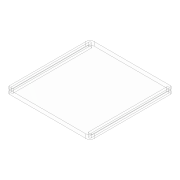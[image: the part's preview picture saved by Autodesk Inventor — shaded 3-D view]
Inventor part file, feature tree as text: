
AUTODESK INVENTOR PART (.ipt)
format: ipt  version: 2020 (Build 240168000, 168)  size: 138,752 bytes
history: native  units: mm
features: sketch x4, extrude x3, fillet x1, plane x1, mirror x1
ambient origin geometry x8: Origin, YZ Plane, XZ Plane, XY Plane, X Axis, Y Axis, Z Axis, Center Point
bodies: Solid1 (feature_tree)
feature tree (10):
  extrude  "Extrusion1"  Depth=105.0mm
  fillet  "Fillet1"  Radius=5.0mm
  sketch  "Sketch3"  dims[d10=5.0mm d11=2.5mm]
  extrude  "Extrusion3"  Depth=2.5mm
  extrude  "Extrusion4"  Depth=2.5mm
  plane  "Work Plane1"
  mirror  "Mirror1"
  sketch  "Sketch1"  dims[d0=105.0mm d1=105.0mm d2=5.0mm d3=0.0mm]
  sketch  "Sketch4"  dims[d12=2.5mm d13=2.5mm]
  sketch  "Sketch5"  dims[d14=2.5mm d15=4.0mm d16=4.0mm d17=4.0mm d18=4.0mm d19=3.0mm d20=3.0mm d21=3.0mm d22=3.0mm d23=10.0mm d24=0.0mm d25=10.0mm d26=0.0mm]
